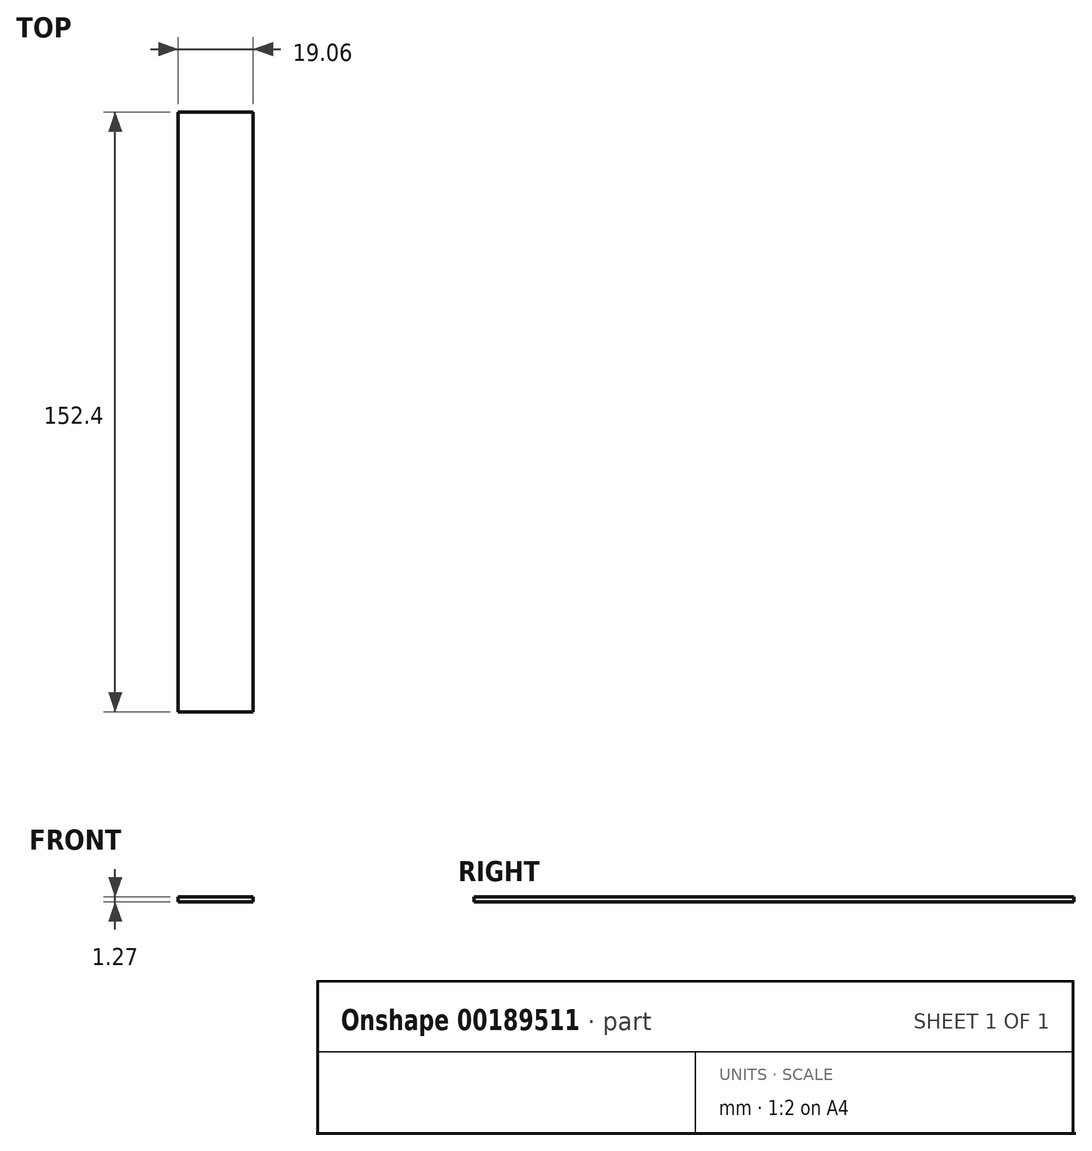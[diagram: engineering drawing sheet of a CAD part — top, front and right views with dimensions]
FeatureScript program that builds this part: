
annotation { "Feature Type Name" : "Feature", "Feature Type Description" : "" }
export const myFeature = defineFeature(function(context is Context, id is Id, definition is map)
    precondition{}
    {
        {
            var Q0;
            Q0=qCreatedBy(makeId("Top.planeOp"),FACE);
            var sketch = newSketch(context, id + "F0", { "sketchPlane" : qUnion([Q0])});
            skLineSegment(sketch, "E0.bottom", {"start": v(-9.52, 76.2) * mm, "end": v(9.53, 76.2) * mm});
            skLineSegment(sketch, "E0.top", {"start": v(-9.53, -76.2) * mm, "end": v(9.52, -76.2) * mm});
            skLineSegment(sketch, "E0.left", {"start": v(-9.52, 76.2) * mm, "end": v(-9.53, -76.2) * mm});
            skLineSegment(sketch, "E0.right", {"start": v(9.53, 76.2) * mm, "end": v(9.52, -76.2) * mm});
            skPoint(sketch, "E0.middle", {"position": v(0, 0) * mm});
            skSolve(sketch);
        }
        {
            var Q0;
            Q0 = qSketchRegion(id + "F0", true);
            extrude(context, id + "F1", {"entities" : qUnion([Q0]), "depth" : 1.27 * mm});
        }
    });
